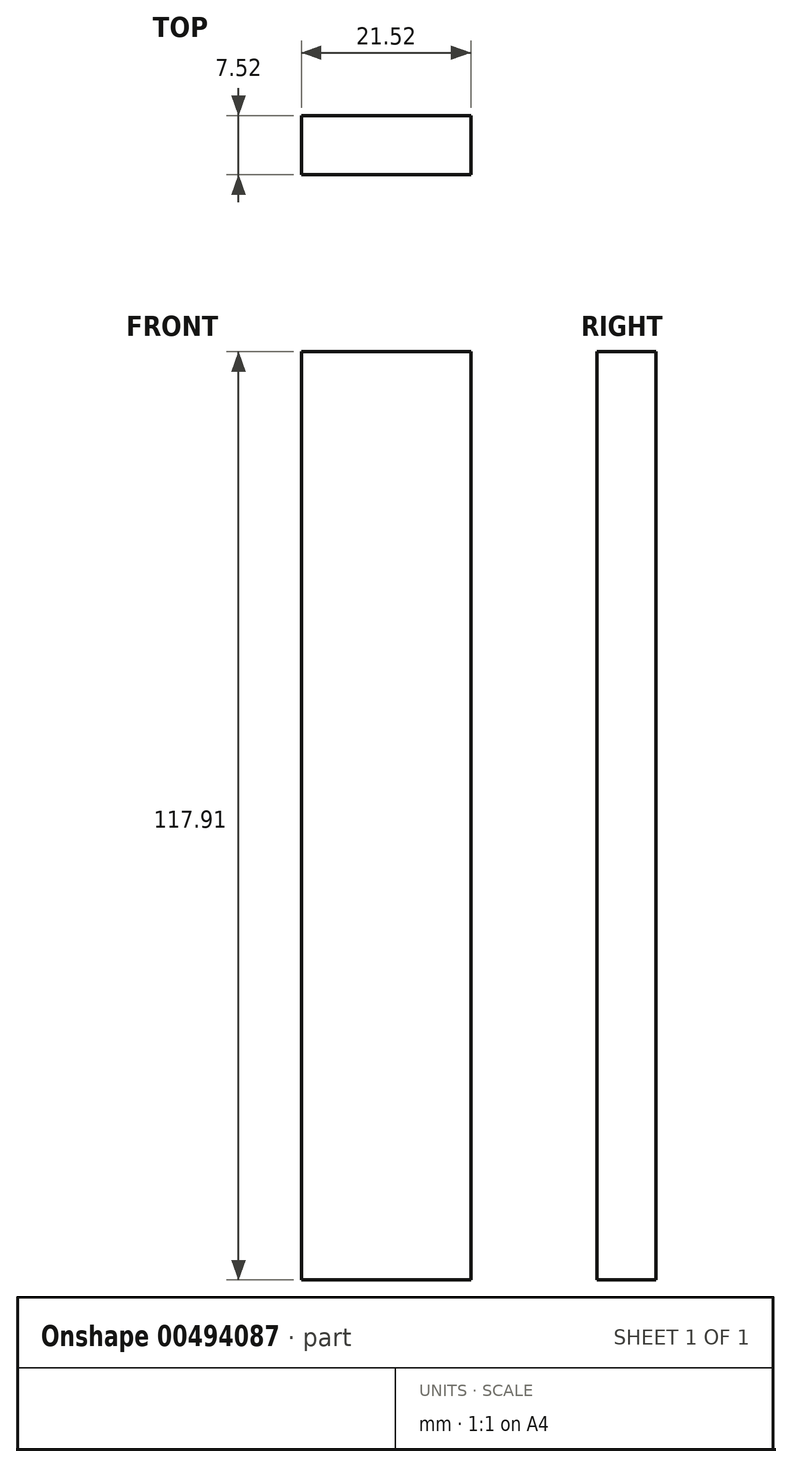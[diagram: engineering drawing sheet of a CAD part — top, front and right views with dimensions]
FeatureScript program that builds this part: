
annotation { "Feature Type Name" : "Feature", "Feature Type Description" : "" }
export const myFeature = defineFeature(function(context is Context, id is Id, definition is map)
    precondition{}
    {
        {
            var Q0;
            Q0=qCreatedBy(makeId("Front.planeOp"),FACE);
            var sketch = newSketch(context, id + "F0", { "sketchPlane" : qUnion([Q0])});
            skLineSegment(sketch, "E0.bottom", {"start": v(-35.27, 54.81) * mm, "end": v(-13.75, 54.81) * mm});
            skLineSegment(sketch, "E0.top", {"start": v(-35.27, -63.1) * mm, "end": v(-13.75, -63.1) * mm});
            skLineSegment(sketch, "E0.left", {"start": v(-35.27, 54.81) * mm, "end": v(-35.27, -63.1) * mm});
            skLineSegment(sketch, "E0.right", {"start": v(-13.75, 54.81) * mm, "end": v(-13.75, -63.1) * mm});
            skSolve(sketch);
        }
        {
            var Q0;
            Q0=makeQuery(id+"F0.imprint","IMPRINT",FACE,{"disambiguationData":[TD([[makeQuery(id+"F0.imprint","IMPRINT",EDGE,{"derivedFrom":sQuery(id+"F0.wireOp",EDGE,"E0.bottom")}),-1.0]])]});
            extrude(context, id + "F1", {"entities" : qUnion([Q0]), "endBound" : BoundingType.SYMMETRIC, "depth" : 7.52 * mm});
        }
    });
